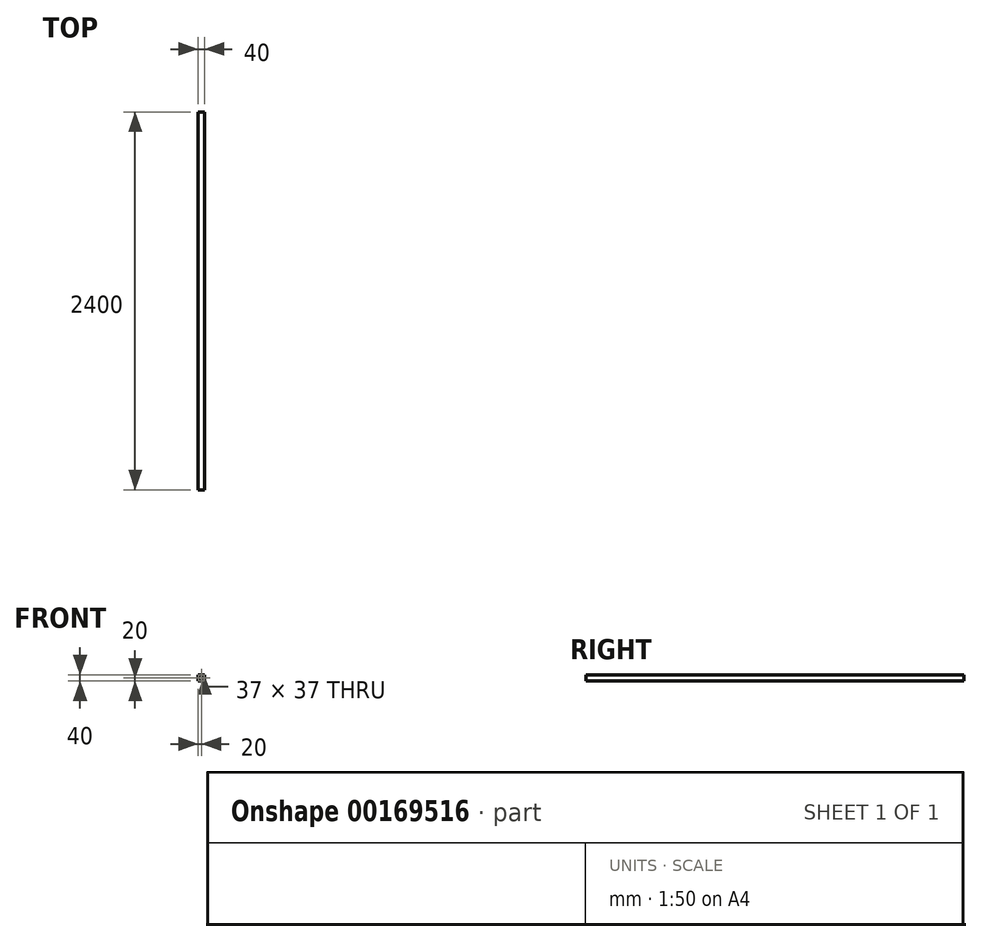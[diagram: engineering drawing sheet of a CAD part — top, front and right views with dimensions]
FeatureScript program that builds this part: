
annotation { "Feature Type Name" : "Feature", "Feature Type Description" : "" }
export const myFeature = defineFeature(function(context is Context, id is Id, definition is map)
    precondition{}
    {
        {
            var Q0;
            Q0=qCreatedBy(makeId("Front.planeOp"),FACE);
            var sketch = newSketch(context, id + "F0", { "sketchPlane" : qUnion([Q0])});
            skLineSegment(sketch, "E0.bottom", {"start": v(20, 20) * mm, "end": v(-20, 20) * mm});
            skLineSegment(sketch, "E0.top", {"start": v(20, -20) * mm, "end": v(-20, -20) * mm});
            skLineSegment(sketch, "E0.left", {"start": v(20, 20) * mm, "end": v(20, -20) * mm});
            skLineSegment(sketch, "E0.right", {"start": v(-20, 20) * mm, "end": v(-20, -20) * mm});
            skPoint(sketch, "E0.middle", {"position": v(0, 0) * mm});
            skLineSegment(sketch, "E1.bottom", {"start": v(18.5, 18.5) * mm, "end": v(-18.5, 18.5) * mm});
            skLineSegment(sketch, "E1.top", {"start": v(18.5, -18.5) * mm, "end": v(-18.5, -18.5) * mm});
            skLineSegment(sketch, "E1.left", {"start": v(18.5, 18.5) * mm, "end": v(18.5, -18.5) * mm});
            skLineSegment(sketch, "E1.right", {"start": v(-18.5, 18.5) * mm, "end": v(-18.5, -18.5) * mm});
            skSolve(sketch);
        }
        {
            var Q0;
            Q0 = qSketchRegion(id + "F0", true);
            extrude(context, id + "F1", {"entities" : qUnion([Q0]), "depth" : 2400 * mm});
        }
    });
